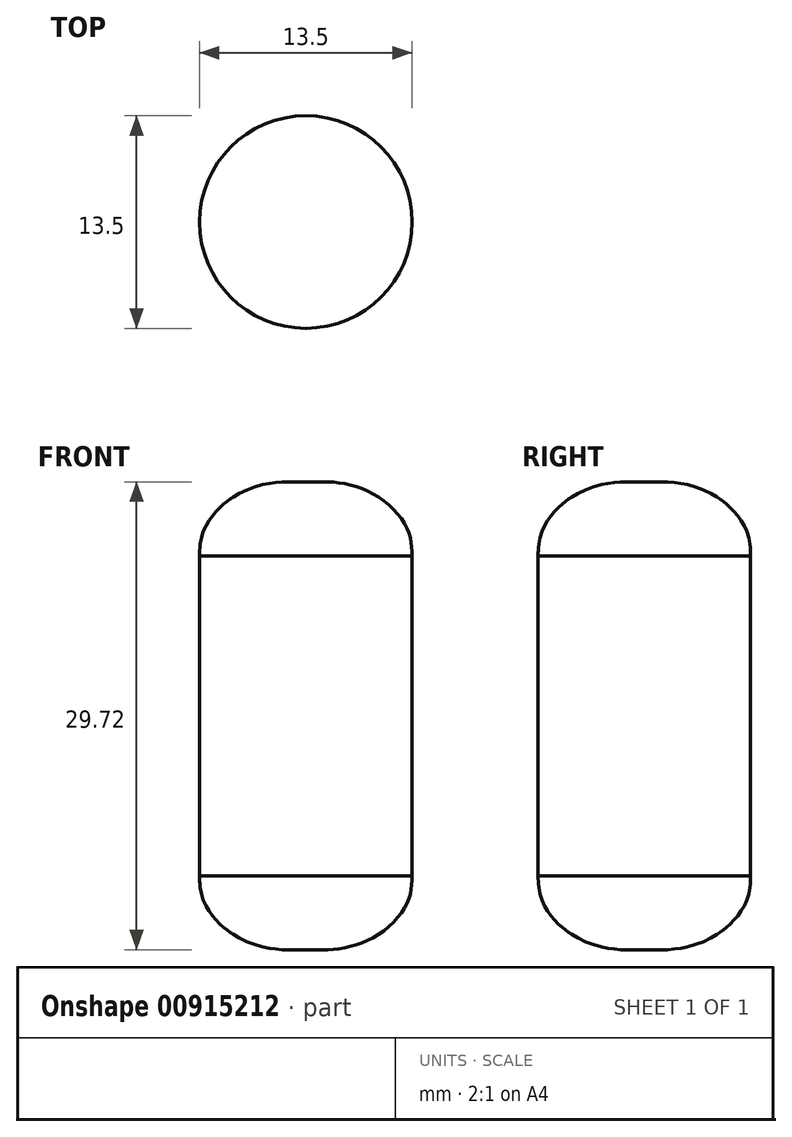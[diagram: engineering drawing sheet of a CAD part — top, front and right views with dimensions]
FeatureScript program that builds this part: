
annotation { "Feature Type Name" : "Feature", "Feature Type Description" : "" }
export const myFeature = defineFeature(function(context is Context, id is Id, definition is map)
    precondition{}
    {
        {
            var Q0;
            Q0=qCreatedBy(makeId("Front.planeOp"),FACE);
            var sketch = newSketch(context, id + "F0", { "sketchPlane" : qUnion([Q0])});
            skLineSegment(sketch, "E0", {"start": v(0, 0) * mm, "end": v(26.33, 0) * mm, "construction": true});
            skLineSegment(sketch, "E1", {"start": v(26.33, 0) * mm, "end": v(-29.15, 0) * mm, "construction": true});
            skPoint(sketch, "E2", {"position": v(6.75, 10.16) * mm});
            skLineSegment(sketch, "E3", {"start": v(6.75, 10.16) * mm, "end": v(6.75, 0) * mm});
            skLineSegment(sketch, "E4", {"start": v(0, 0) * mm, "end": v(0, 14.82) * mm, "construction": true});
            skFitSpline(sketch, "E5", {"points": [v(0, 14.82) * mm, v(1.96, 14.82) * mm, v(4.62, 13.89) * mm, v(6.48, 11.8) * mm, v(6.75, 10.16) * mm], "startDerivative": vector(8.08, 0.54) * mm, "endDerivative": vector(0.2, -7.52) * mm});
            skLineSegment(sketch, "E6", {"start": v(6.75, 0) * mm, "end": v(0, 0) * mm});
            skLineSegment(sketch, "E7", {"start": v(0, 14.82) * mm, "end": v(0, 0) * mm});
            skLineSegment(sketch, "E8.MirrorCS", {"start": v(0, -14.82) * mm, "end": v(0, 0) * mm});
            skLineSegment(sketch, "E9.MirrorCS", {"start": v(6.75, -10.16) * mm, "end": v(6.75, 0) * mm});
            skPoint(sketch, "E10.MirrorP", {"position": v(6.75, -10.16) * mm});
            skFitSpline(sketch, "E11.MirrorCS", {"points": [v(0, -14.82) * mm, v(1.96, -14.82) * mm, v(4.62, -13.89) * mm, v(6.48, -11.8) * mm, v(6.75, -10.16) * mm], "startDerivative": vector(8.08, -0.54) * mm, "endDerivative": vector(0.2, 7.52) * mm});
            skSolve(sketch);
        }
        {
            var Q0;
            Q0 = qSketchRegion(id + "F0", true);
            var Q1;
            Q1=sQuery(id+"F0.wireOp",EDGE,"E8.MirrorCS");
            revolve(context, id + "F1", {"surfaceOperationType" : NewSurfaceOperationType.NEW, "entities" : qUnion([Q0]), "axis" : qUnion([Q1]), "revolveType" : RevolveType.FULL});
        }
    });
